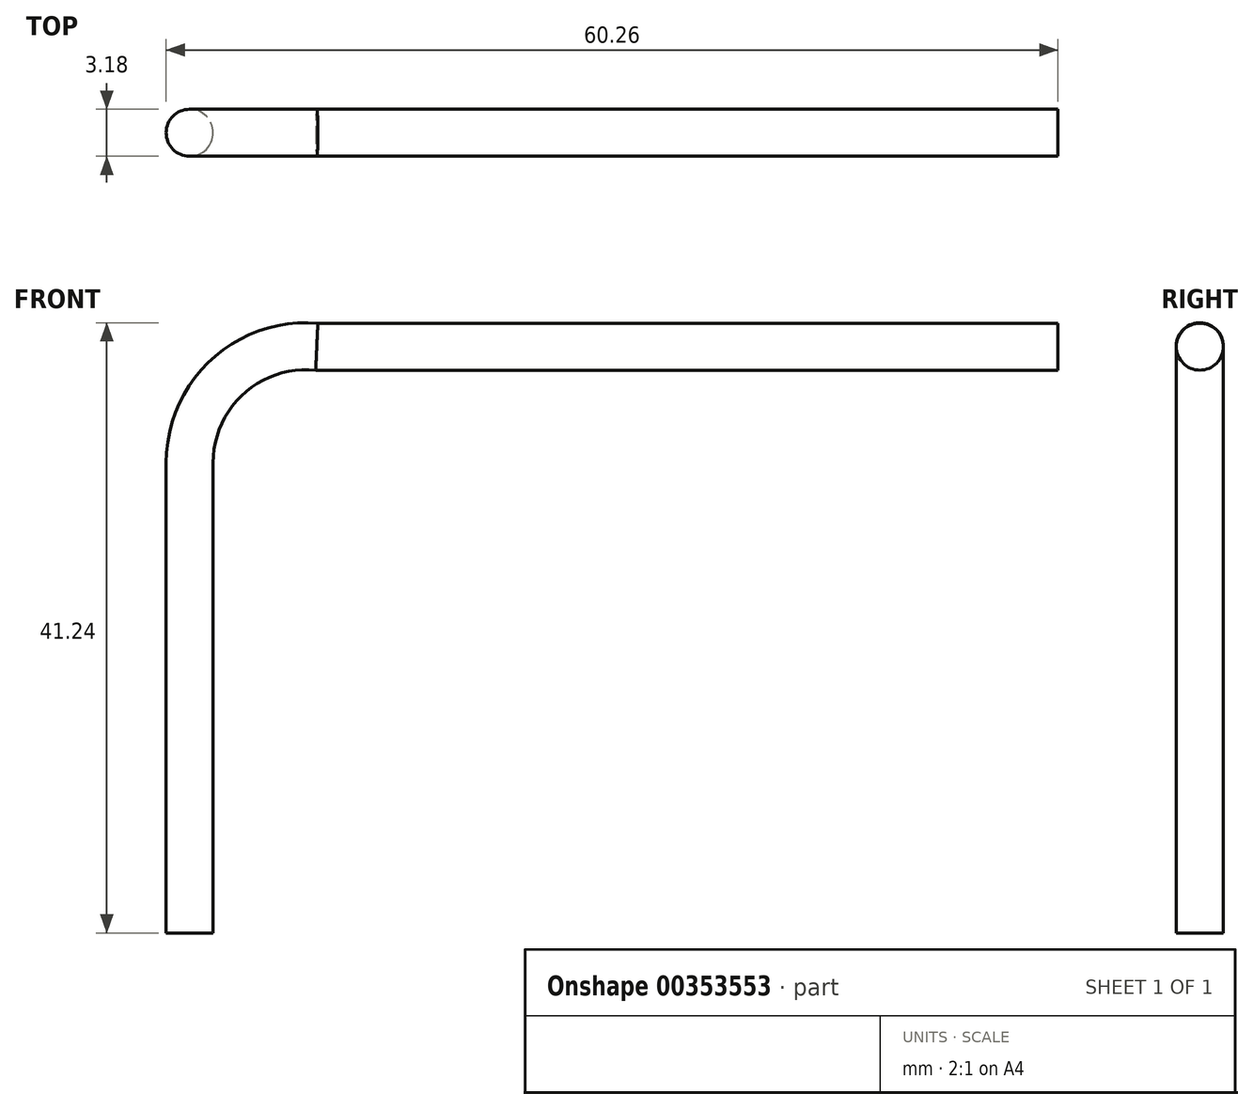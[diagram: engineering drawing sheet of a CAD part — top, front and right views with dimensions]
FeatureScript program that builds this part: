
annotation { "Feature Type Name" : "Feature", "Feature Type Description" : "" }
export const myFeature = defineFeature(function(context is Context, id is Id, definition is map)
    precondition{}
    {
        {
            var Q0;
            Q0=qCreatedBy(makeId("Top.planeOp"),FACE);
            var sketch = newSketch(context, id + "F0", { "sketchPlane" : qUnion([Q0])});
            skCircle(sketch, "E0", {"center": v(0, 0) * mm, "radius": 1.59 * mm});
            skSolve(sketch);
        }
        {
            var Q0;
            Q0=qCreatedBy(makeId("Front.planeOp"),FACE);
            var sketch = newSketch(context, id + "F1", { "sketchPlane" : qUnion([Q0])});
            skLineSegment(sketch, "E1", {"start": v(0, 0) * mm, "end": v(0, 31.78) * mm});
            skArc(sketch, "E2", {"start": v(8.6, 39.62) * mm, "mid": v(2.57, 37.6) * mm, "end": v(0, 31.78) * mm});
            skLineSegment(sketch, "E3", {"start": v(8.6, 39.62) * mm, "end": v(58.67, 39.62) * mm});
            skSolve(sketch);
        }
        {
            var Q0;
            Q0 = qSketchRegion(id + "F0", true);
            var Q1;
            Q1 = qConstructionFilter(qBodyType(qCreatedBy(id + "F1" ,EDGE), BodyType.WIRE), ConstructionObject.NO);
            sweep(context, id + "F2", {"profiles" : qUnion([Q0]), "path" : qUnion([Q1])});
        }
    });
